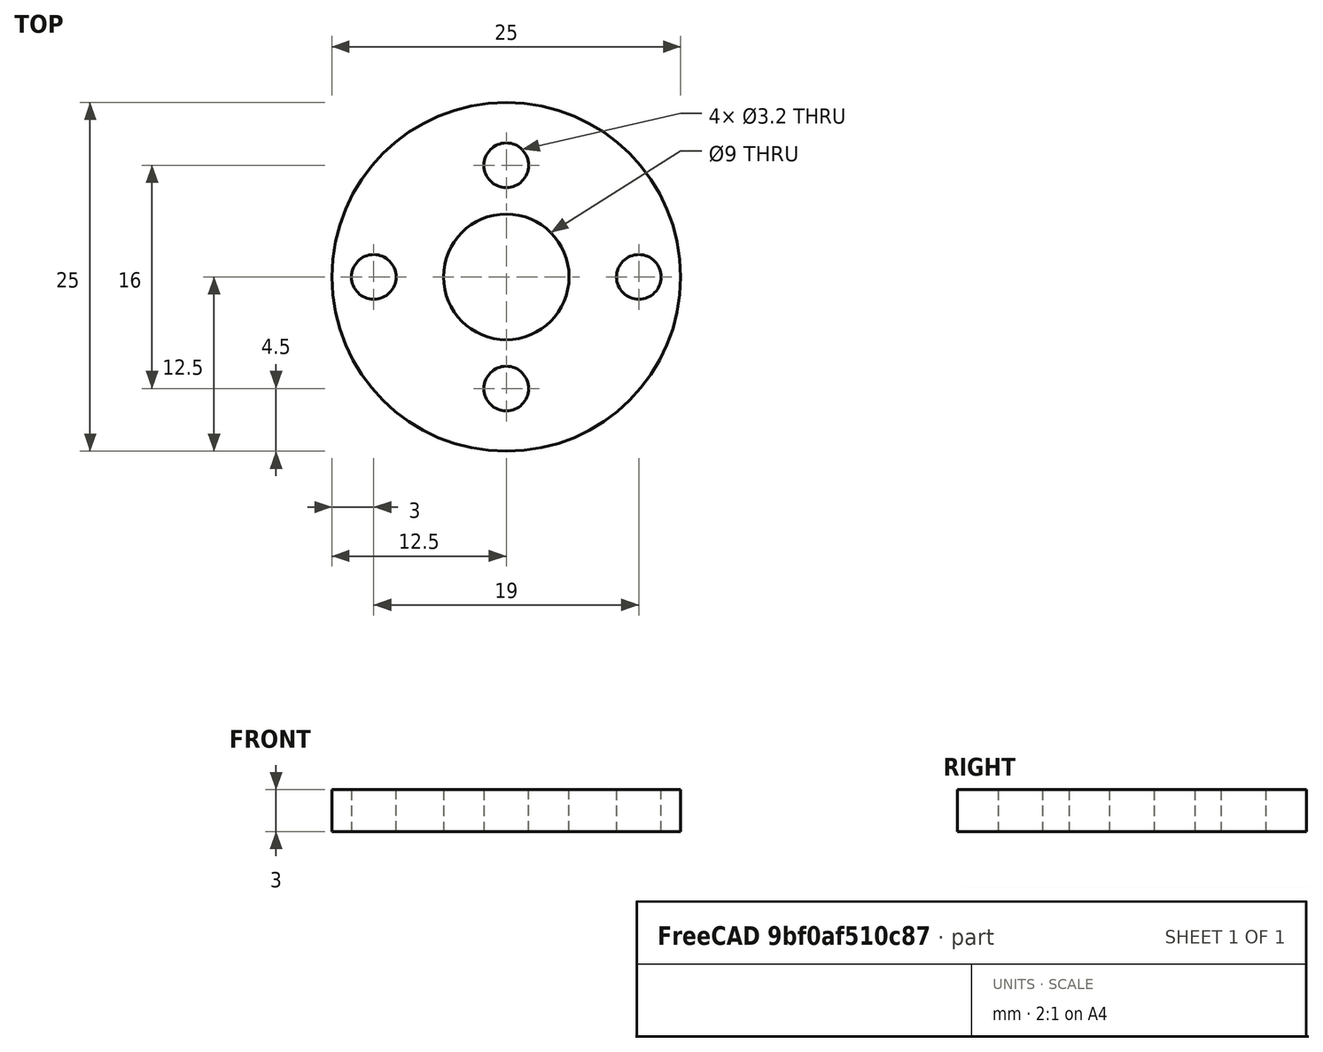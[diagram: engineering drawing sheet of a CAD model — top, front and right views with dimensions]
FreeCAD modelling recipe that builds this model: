
FCSTD DOCUMENT  (FreeCAD 0.19R24276 (Git))
Label: Bldc_holder
License: All rights reserved
LicenseURL: http://en.wikipedia.org/wiki/All_rights_reserved
objects: Sketcher::SketchObject×1, PartDesign::Pad×1, PartDesign::Body×1
note: 4 computed .brp shape members not serialized (recipe doc carries the construction recipe); baked Part::Feature solids carry a one-line shape summary decoded from their .brp

FEATURE [Sketcher::SketchObject] Sketch
  FullyConstrained = false
  MapMode = 5
  Support = -> [XY_Plane]
  sketch-geometry (6):
    g0: Circle CenterX=0 CenterY=8 CenterZ=0 NormalX=0 NormalY=0 NormalZ=1 AngleXU=0 Radius=1.6
    g1: Circle CenterX=0 CenterY=-8 CenterZ=0 NormalX=0 NormalY=0 NormalZ=1 AngleXU=0 Radius=1.6
    g2: Circle CenterX=9.5 CenterY=0 CenterZ=0 NormalX=0 NormalY=0 NormalZ=1 AngleXU=0 Radius=1.6
    g3: Circle CenterX=-9.5 CenterY=0 CenterZ=0 NormalX=0 NormalY=0 NormalZ=1 AngleXU=0 Radius=1.6
    g4: Circle CenterX=0 CenterY=0 CenterZ=0 NormalX=0 NormalY=0 NormalZ=1 AngleXU=0 Radius=12.5
    g5: Circle CenterX=0 CenterY=0 CenterZ=0 NormalX=0 NormalY=0 NormalZ=1 AngleXU=0 Radius=4.5
  constraints (15):
    c: PointOnObject(g0,g-2)
    c: Diameter(g0) = 3.2
    c: PointOnObject(g1,g-2)
    c: DistanceY(g1,g-1) = 8
    c: PointOnObject(g2,g-1)
    c: PointOnObject(g3,g-1)
    c: DistanceX(g-1,g2) = 9.5
    c: DistanceX(g3,g-1) = 9.5
    c: Equal(g3,g1)
    c: Equal(g1,g2)
    c: Equal(g2,g0)
    c: Coincident(g4,g-1)
    c: Diameter(g4) = 25
    c: Coincident(g5,g4)
    c: Diameter(g5) = 9
FEATURE [PartDesign::Pad] Pad
  Direction = (1,1,1)
  Length = 3
  Length2 = 100
  Profile = -> Sketch
  Type = 0
FEATURE [PartDesign::Body] Body
  Group = -> [Sketch,Pad]
  Origin = -> Origin
  Tip = -> Pad
